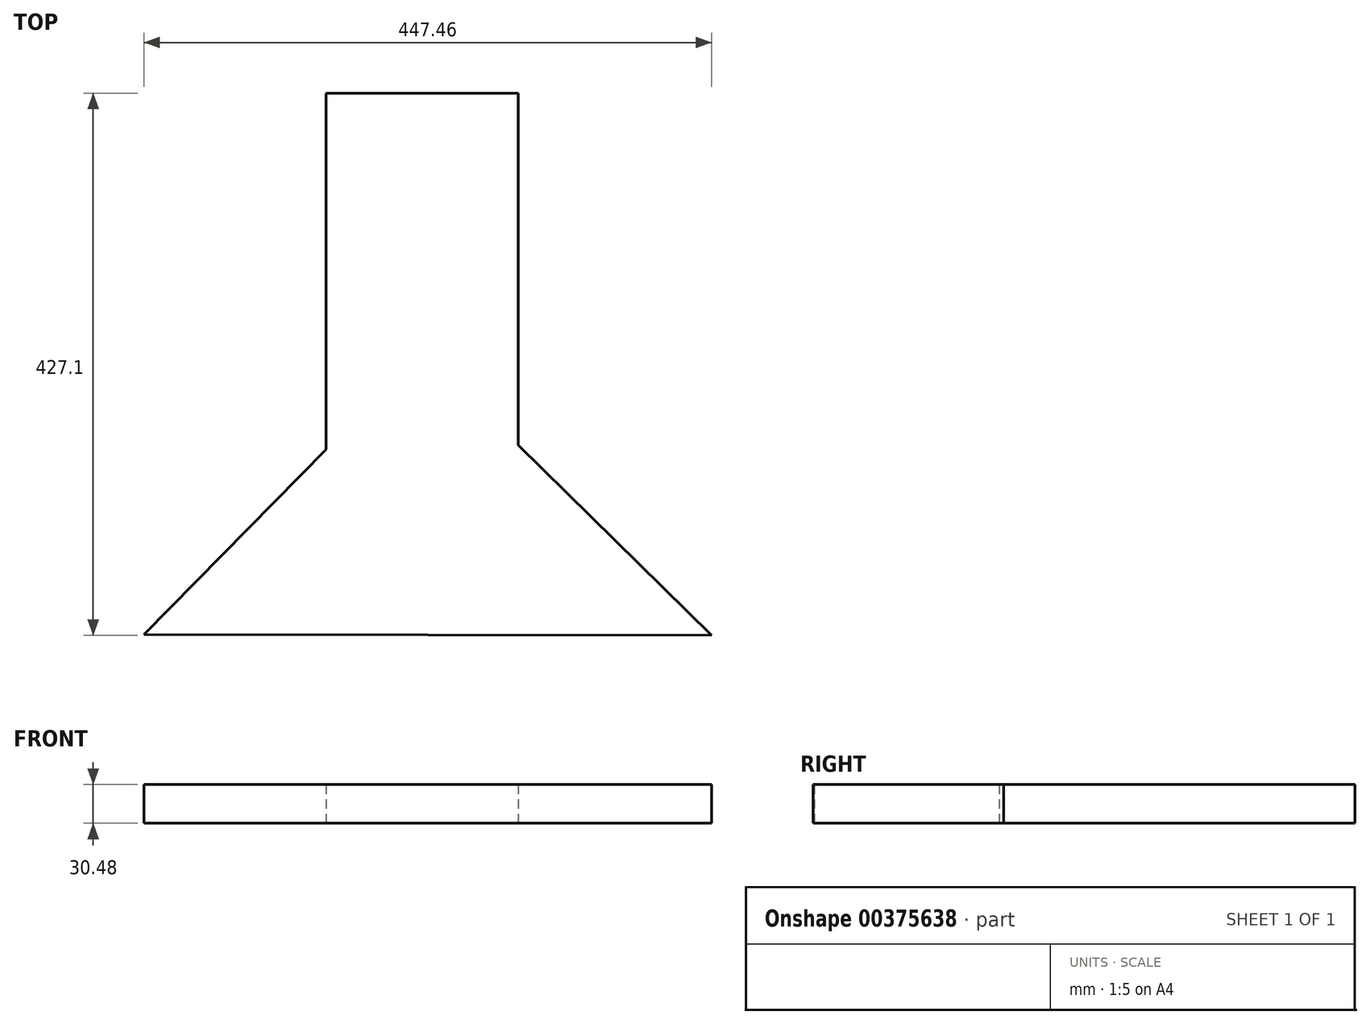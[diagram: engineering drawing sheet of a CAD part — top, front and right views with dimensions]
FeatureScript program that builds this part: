
annotation { "Feature Type Name" : "Feature", "Feature Type Description" : "" }
export const myFeature = defineFeature(function(context is Context, id is Id, definition is map)
    precondition{}
    {
        {
            var Q0;
            Q0=qCreatedBy(makeId("Top.planeOp"),FACE);
            var sketch = newSketch(context, id + "F0", { "sketchPlane" : qUnion([Q0])});
            skLineSegment(sketch, "E0", {"start": v(0, 0) * mm, "end": v(-219.7, -223.34) * mm});
            skLineSegment(sketch, "E1", {"start": v(0, 0) * mm, "end": v(227.75, -224.04) * mm});
            skLineSegment(sketch, "E2", {"start": v(227.75, -224.04) * mm, "end": v(-219.7, -223.34) * mm});
            skLineSegment(sketch, "E3", {"start": v(-76.33, -77.6) * mm, "end": v(-76.33, 203.06) * mm});
            skLineSegment(sketch, "E4", {"start": v(-76.33, 203.06) * mm, "end": v(75.18, 203.06) * mm});
            skLineSegment(sketch, "E5", {"start": v(75.18, 203.06) * mm, "end": v(75.18, -73.95) * mm});
            skSolve(sketch);
        }
        {
            var Q0;
            Q0 = qSketchRegion(id + "F0", true);
            extrude(context, id + "F1", {"entities" : qUnion([Q0]), "depth" : 30.48 * mm});
        }
    });
